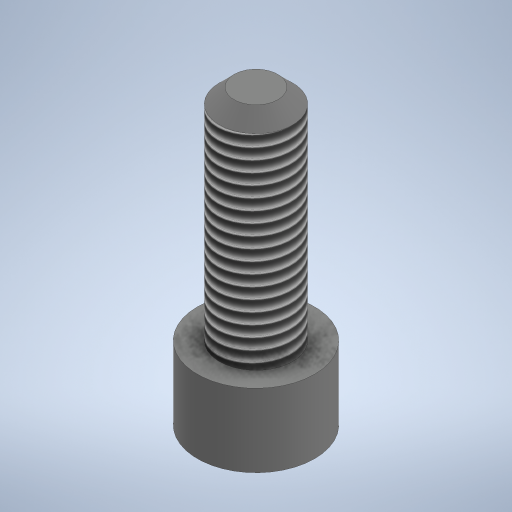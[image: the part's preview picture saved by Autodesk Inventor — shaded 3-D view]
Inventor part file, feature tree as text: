
AUTODESK INVENTOR PART (.ipt)
format: ipt  version: 2023 (Build 270158000, 158)  size: 308,224 bytes
history: native  units: mm
features: extrude x3, sketch x3, other x2, chamfer x1
ambient origin geometry x8: Origin, YZ Plane, XZ Plane, XY Plane, X Axis, Y Axis, Z Axis, Center Point
bodies: Body1 (feature_tree)
feature tree (9):
  other  "솔리드1"
  extrude  "돌출1"  Depth=10.0mm
  extrude  "돌출2"  Depth=30.0mm TaperAngle=0.0deg
  extrude  "돌출3"  Depth=16.0mm
  chamfer  "모따기1"  Distance=10.0mm
  other  "스레드1"
  sketch  "스케치1"
  sketch  "스케치2"
  sketch  "스케치3"
